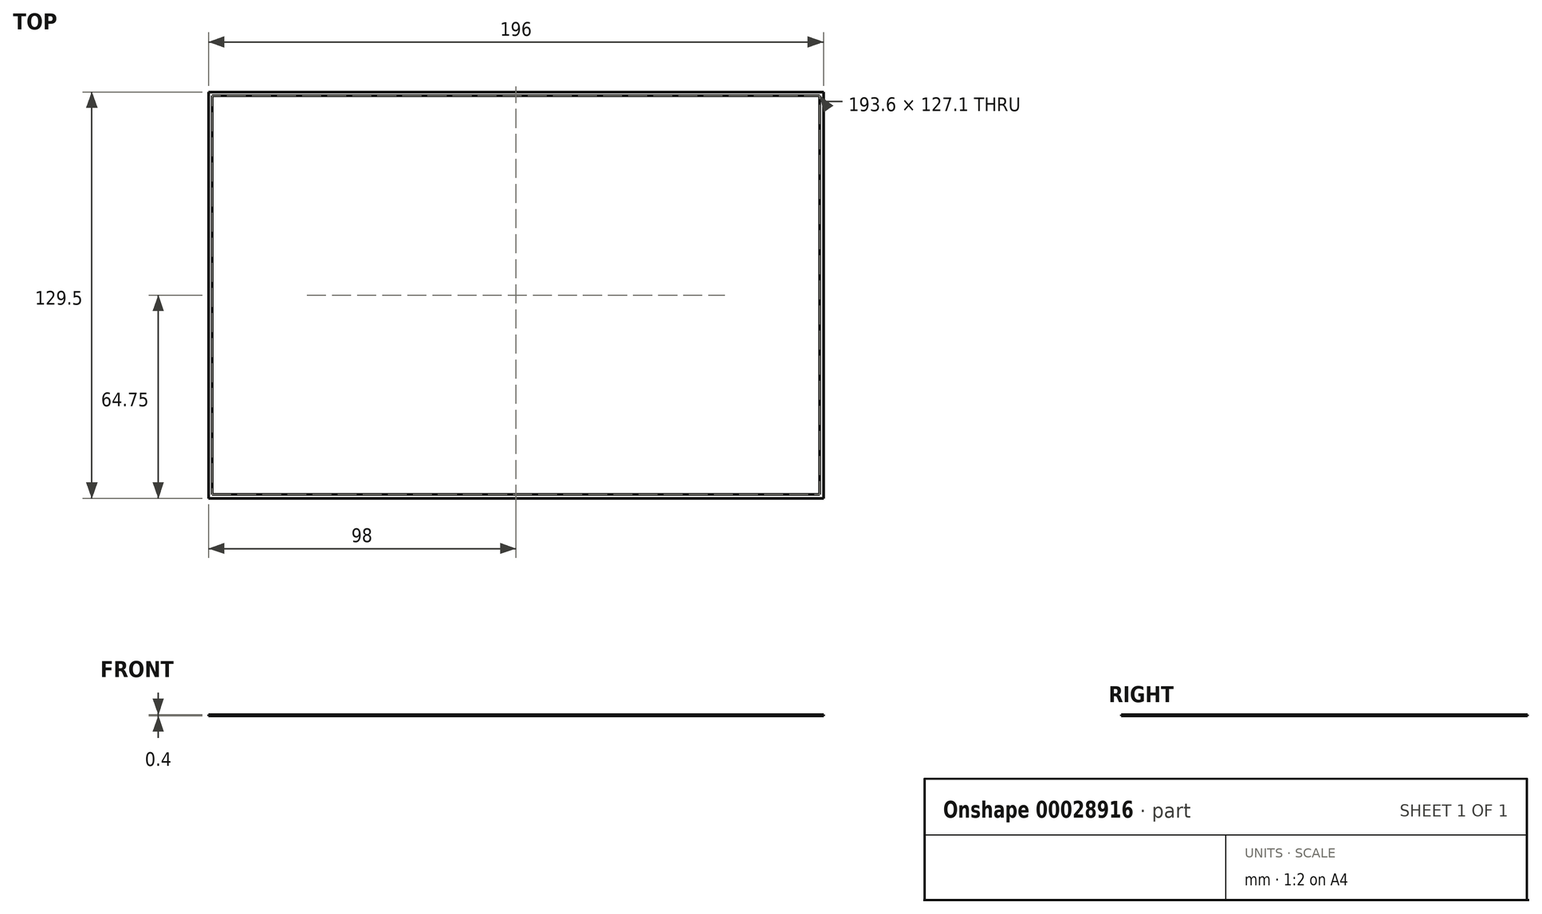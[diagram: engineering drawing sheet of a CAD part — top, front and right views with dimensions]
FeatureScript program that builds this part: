
annotation { "Feature Type Name" : "Feature", "Feature Type Description" : "" }
export const myFeature = defineFeature(function(context is Context, id is Id, definition is map)
    precondition{}
    {
        {
            var Q0;
            Q0=qCreatedBy(makeId("Top.planeOp"),FACE);
            var sketch = newSketch(context, id + "F0", { "sketchPlane" : qUnion([Q0])});
            skLineSegment(sketch, "E0.bottom", {"start": v(0, 129.5) * mm, "end": v(196, 129.5) * mm});
            skLineSegment(sketch, "E0.top", {"start": v(0, 0) * mm, "end": v(196, 0) * mm});
            skLineSegment(sketch, "E0.left", {"start": v(0, 129.5) * mm, "end": v(0, 0) * mm});
            skLineSegment(sketch, "E0.right", {"start": v(196, 129.5) * mm, "end": v(196, 0) * mm});
            skLineSegment(sketch, "E1.bottom", {"start": v(1.2, 128.3) * mm, "end": v(194.8, 128.3) * mm});
            skLineSegment(sketch, "E1.top", {"start": v(1.2, 1.2) * mm, "end": v(194.8, 1.2) * mm});
            skLineSegment(sketch, "E1.left", {"start": v(1.2, 128.3) * mm, "end": v(1.2, 1.2) * mm});
            skLineSegment(sketch, "E1.right", {"start": v(194.8, 128.3) * mm, "end": v(194.8, 1.2) * mm});
            skSolve(sketch);
        }
        {
            var Q0;
            Q0=makeQuery(id+"F0.imprint","IMPRINT",FACE,{"disambiguationData":[TD([[makeQuery(id+"F0.imprint","IMPRINT",EDGE,{"derivedFrom":sQuery(id+"F0.wireOp",EDGE,"E0.bottom")}),-1.0]])]});
            extrude(context, id + "F1", {"entities" : qUnion([Q0]), "oppositeDirection" : true, "depth" : 0.4 * mm});
        }
    });
